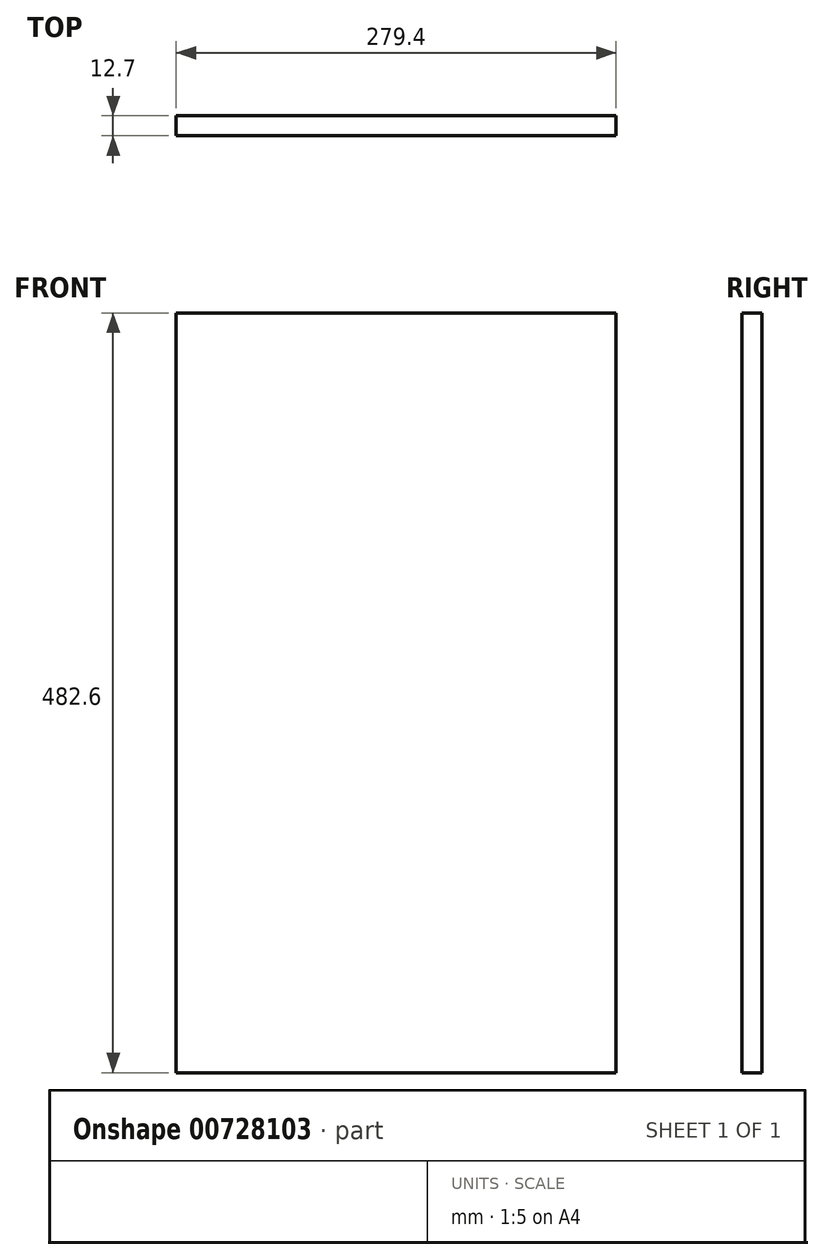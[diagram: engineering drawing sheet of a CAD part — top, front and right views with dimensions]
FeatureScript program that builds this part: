
annotation { "Feature Type Name" : "Feature", "Feature Type Description" : "" }
export const myFeature = defineFeature(function(context is Context, id is Id, definition is map)
    precondition{}
    {
        {
            var Q0;
            Q0=qCreatedBy(makeId("Front.planeOp"),FACE);
            var sketch = newSketch(context, id + "F0", { "sketchPlane" : qUnion([Q0])});
            skLineSegment(sketch, "E0.bottom", {"start": v(-124.68, 273.27) * mm, "end": v(154.72, 273.27) * mm});
            skLineSegment(sketch, "E0.top", {"start": v(-124.68, -209.33) * mm, "end": v(154.72, -209.33) * mm});
            skLineSegment(sketch, "E0.left", {"start": v(-124.68, 273.27) * mm, "end": v(-124.68, -209.33) * mm});
            skLineSegment(sketch, "E0.right", {"start": v(154.72, 273.27) * mm, "end": v(154.72, -209.33) * mm});
            skSolve(sketch);
        }
        {
            var Q0;
            Q0=makeQuery(id+"F0.imprint","IMPRINT",FACE,{"disambiguationData":[TD([[makeQuery(id+"F0.imprint","IMPRINT",EDGE,{"derivedFrom":sQuery(id+"F0.wireOp",EDGE,"E0.bottom")}),-1.0]])]});
            extrude(context, id + "F1", {"entities" : qUnion([Q0]), "depth" : 12.7 * mm, "offsetDistance" : 25.4 * mm});
        }
    });
